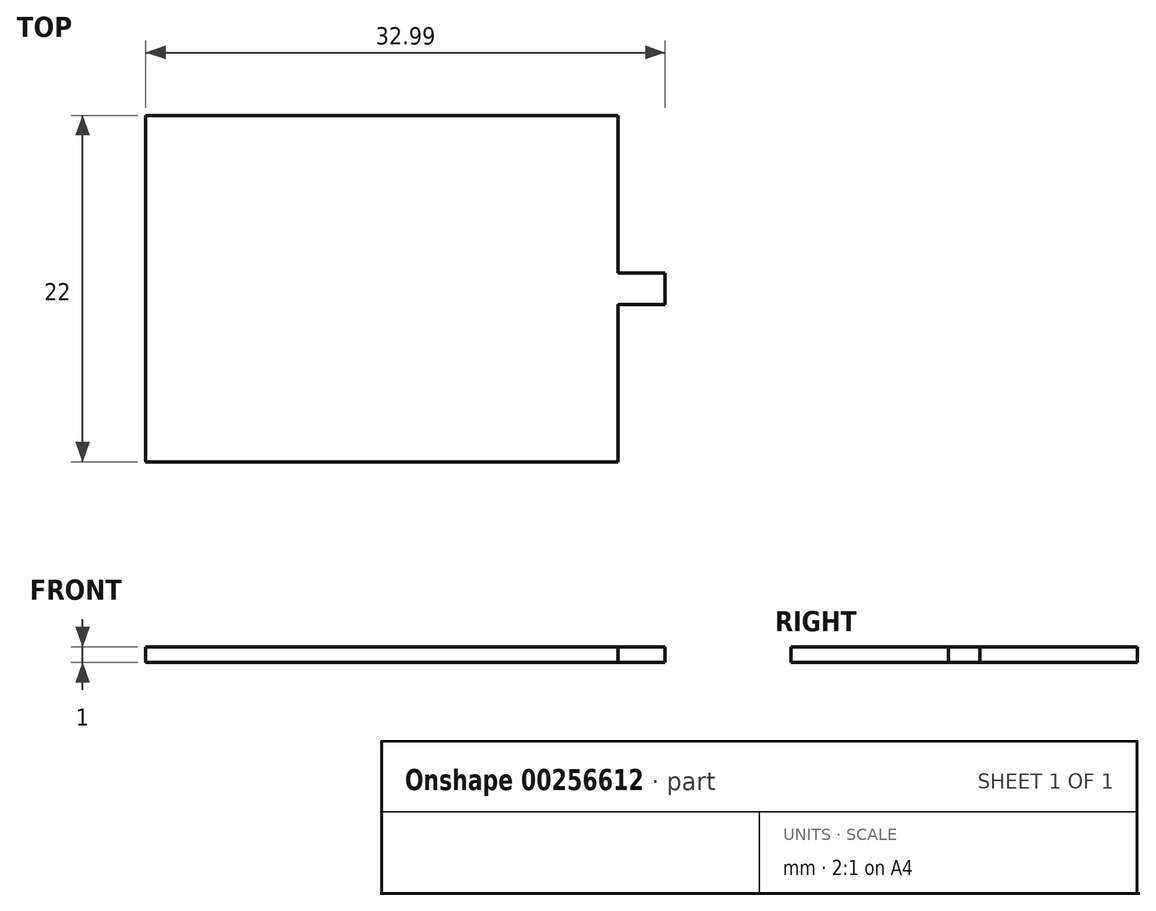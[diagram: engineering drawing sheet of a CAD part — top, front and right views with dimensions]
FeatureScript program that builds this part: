
annotation { "Feature Type Name" : "Feature", "Feature Type Description" : "" }
export const myFeature = defineFeature(function(context is Context, id is Id, definition is map)
    precondition{}
    {
        {
            var Q0;
            Q0=qCreatedBy(makeId("Top.planeOp"),FACE);
            var sketch = newSketch(context, id + "F0", { "sketchPlane" : qUnion([Q0])});
            skLineSegment(sketch, "E0", {"start": v(2.99, 0) * mm, "end": v(2.99, 1) * mm});
            skLineSegment(sketch, "E1", {"start": v(2.99, 1) * mm, "end": v(0, 1) * mm});
            skLineSegment(sketch, "E2", {"start": v(0, 1) * mm, "end": v(0, 11) * mm});
            skLineSegment(sketch, "E3", {"start": v(0, 11) * mm, "end": v(-30, 11) * mm});
            skLineSegment(sketch, "E4", {"start": v(-30, 11) * mm, "end": v(-30, -11) * mm});
            skLineSegment(sketch, "E5", {"start": v(-30, -11) * mm, "end": v(0, -11) * mm});
            skLineSegment(sketch, "E6", {"start": v(0, -11) * mm, "end": v(0, -1) * mm});
            skLineSegment(sketch, "E7", {"start": v(0, -1) * mm, "end": v(2.99, -1) * mm});
            skLineSegment(sketch, "E8", {"start": v(2.99, -1) * mm, "end": v(2.99, 0) * mm});
            skSolve(sketch);
        }
        {
            var Q0;
            Q0=makeQuery(id+"F0.imprint","IMPRINT",FACE,{"disambiguationData":[TD([[makeQuery(id+"F0.imprint","IMPRINT",EDGE,{"derivedFrom":sQuery(id+"F0.wireOp",EDGE,"E0")}),1.0]])]});
            extrude(context, id + "F1", {"entities" : qUnion([Q0]), "depth" : 1 * mm});
        }
    });
